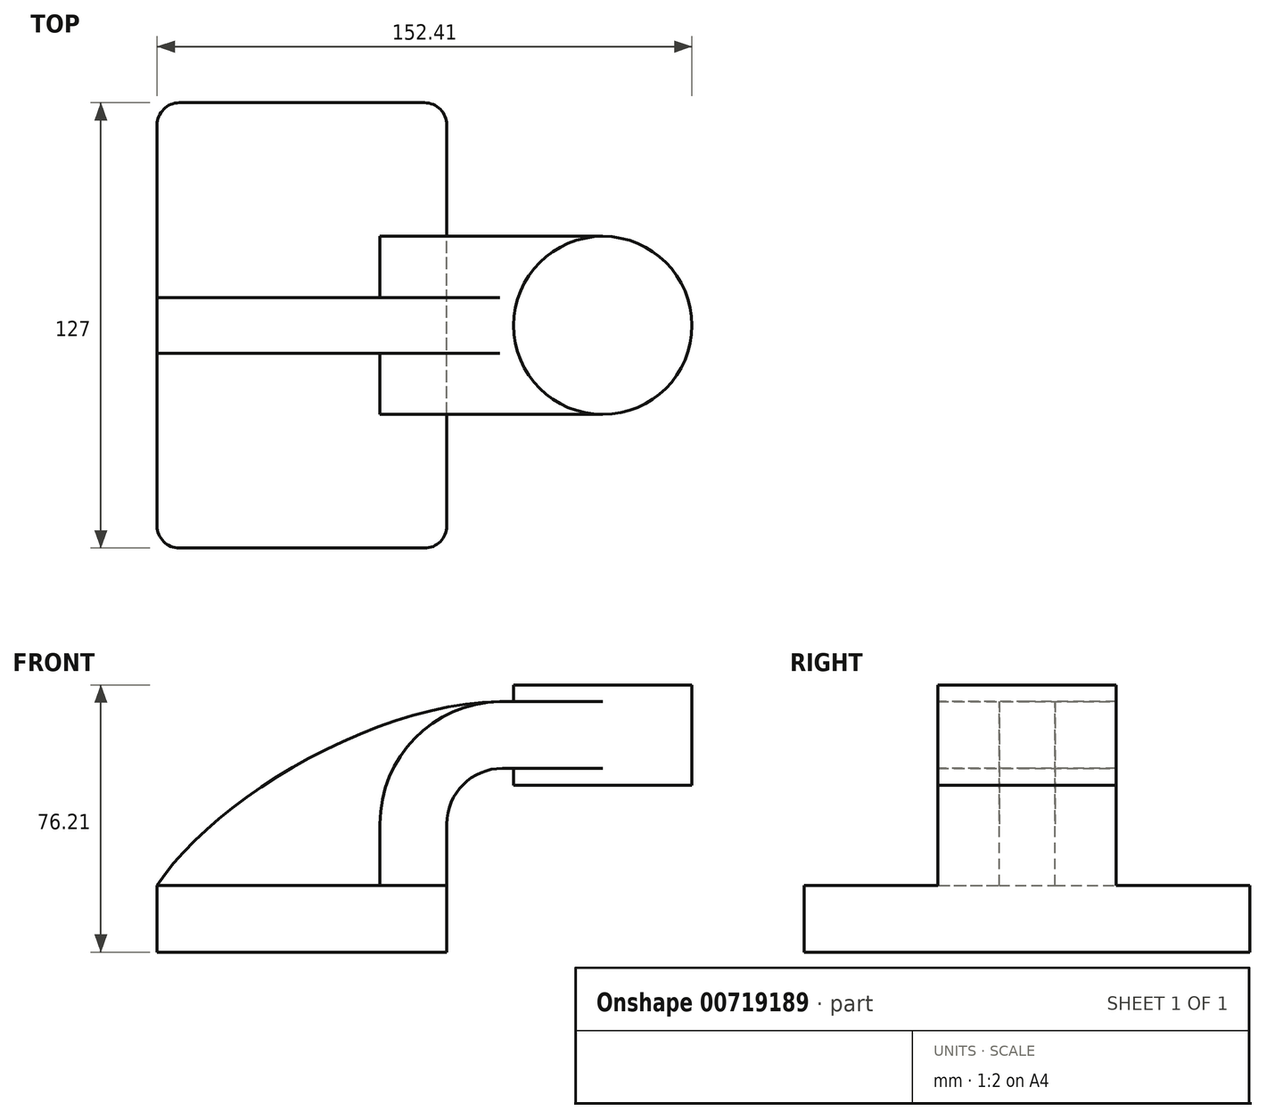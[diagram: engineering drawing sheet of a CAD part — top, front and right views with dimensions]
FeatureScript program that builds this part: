
annotation { "Feature Type Name" : "Feature", "Feature Type Description" : "" }
export const myFeature = defineFeature(function(context is Context, id is Id, definition is map)
    precondition{}
    {
        {
            var Q0;
            Q0=qCreatedBy(makeId("Front.planeOp"),FACE);
            var sketch = newSketch(context, id + "F0", { "sketchPlane" : qUnion([Q0])});
            skLineSegment(sketch, "E0.bottom", {"start": v(-41.28, 9.52) * mm, "end": v(41.27, 9.53) * mm});
            skLineSegment(sketch, "E0.top", {"start": v(-41.28, -9.53) * mm, "end": v(41.28, -9.53) * mm});
            skLineSegment(sketch, "E0.left", {"start": v(-41.28, 9.52) * mm, "end": v(-41.27, -9.53) * mm});
            skLineSegment(sketch, "E0.right", {"start": v(41.28, 9.53) * mm, "end": v(41.28, -9.52) * mm});
            skPoint(sketch, "E0.middle", {"position": v(0, 0) * mm});
            skLineSegment(sketch, "E1.bottom", {"start": v(111.12, 38.1) * mm, "end": v(60.32, 38.1) * mm});
            skLineSegment(sketch, "E1.top", {"start": v(111.12, 66.68) * mm, "end": v(60.32, 66.67) * mm});
            skLineSegment(sketch, "E1.left", {"start": v(111.12, 38.1) * mm, "end": v(111.12, 66.68) * mm});
            skLineSegment(sketch, "E1.right", {"start": v(60.32, 38.1) * mm, "end": v(60.32, 66.67) * mm});
            skPoint(sketch, "E1.middle", {"position": v(85.72, 52.39) * mm});
            skLineSegment(sketch, "E2", {"start": v(41.27, 9.53) * mm, "end": v(41.27, 27) * mm});
            skArc(sketch, "E3", {"start": v(41.27, 27) * mm, "mid": v(45.92, 38.23) * mm, "end": v(57.15, 42.88) * mm});
            skLineSegment(sketch, "E4", {"start": v(57.15, 42.88) * mm, "end": v(85.72, 42.88) * mm});
            skArc(sketch, "E5.0", {"start": v(22.22, 27) * mm, "mid": v(32.45, 51.7) * mm, "end": v(57.15, 61.93) * mm});
            skLineSegment(sketch, "E5.1", {"start": v(22.22, 9.53) * mm, "end": v(22.22, 27) * mm});
            skLineSegment(sketch, "E6.0", {"start": v(57.15, 61.93) * mm, "end": v(85.73, 61.93) * mm});
            skLineSegment(sketch, "E7", {"start": v(85.72, 38.1) * mm, "end": v(85.72, 66.68) * mm});
            skFitSpline(sketch, "E8", {"points": [v(-41.28, 9.52) * mm, v(57.15, 61.93) * mm], "startDerivative": vector(47.24, 72.44) * mm, "endDerivative": vector(110, 0.7) * mm});
            skSolve(sketch);
        }
        {
            var Q0;
            Q0=makeQuery(id+"F0.imprint","IMPRINT",FACE,{"disambiguationData":[TD([[makeQuery(id+"F0.imprint","IMPRINT",EDGE,{"derivedFrom":sQuery(id+"F0.wireOp",EDGE,"E0.top")}),1.0]])]});
            extrude(context, id + "F1", {"entities" : qUnion([Q0]), "endBound" : BoundingType.SYMMETRIC, "depth" : 127 * mm, "offsetDistance" : 25.4 * mm});
        }
        {
            var Q0;
            {var subQ1=sQuery(id+"F0.wireOp",EDGE,"E2");Q0=makeQuery(id+"F0.imprint","IMPRINT",FACE,{"disambiguationData":[TD([[makeQuery(id+"F0.imprint","IMPRINT",EDGE,{"derivedFrom":subQ1}),1.0]])]});}
            var Q1;
            {var subQ0=sQuery(id+"F0.wireOp",EDGE,"E4");var subQ1=sQuery(id+"F0.wireOp",EDGE,"E1.right");var subQ2=makeQuery(id+"F0.imprint","INTERSECT",VERTEX,{"derivedFrom":[subQ1,subQ0]});Q1=makeQuery(id+"F0.imprint","IMPRINT",FACE,{"disambiguationData":[TD([[makeQuery(id+"F0.imprint","IMPRINT",EDGE,{"disambiguationData":[TD([[subQ2,-1.0]])],"derivedFrom":subQ1}),-1.0]])]});}
            extrude(context, id + "F2", {"entities" : qUnion([Q0, Q1]), "operationType" : NewBodyOperationType.ADD, "endBound" : BoundingType.SYMMETRIC, "depth" : 50.8 * mm, "offsetDistance" : 25.4 * mm});
        }
        {
            var Q0;
            {var subQ3=sQuery(id+"F0.wireOp",EDGE,"E5.1");Q0=makeQuery(id+"F0.imprint","IMPRINT",FACE,{"disambiguationData":[TD([[makeQuery(id+"F0.imprint","IMPRINT",EDGE,{"derivedFrom":subQ3}),1.0]])]});}
            extrude(context, id + "F3", {"entities" : qUnion([Q0]), "operationType" : NewBodyOperationType.ADD, "endBound" : BoundingType.SYMMETRIC, "depth" : 15.88 * mm, "offsetDistance" : 25.4 * mm});
        }
        {
            var Q0;
            {var subQ0=sQuery(id+"F0.wireOp",EDGE,"E1.left");Q0=makeQuery(id+"F0.imprint","IMPRINT",FACE,{"disambiguationData":[TD([[makeQuery(id+"F0.imprint","IMPRINT",EDGE,{"derivedFrom":subQ0}),1.0]])]});}
            var Q1;
            Q1=sQuery(id+"F0.wireOp",EDGE,"E7");
            revolve(context, id + "F4", {"operationType" : NewBodyOperationType.ADD, "surfaceOperationType" : NewSurfaceOperationType.NEW, "entities" : qUnion([Q0]), "axis" : qUnion([Q1]), "revolveType" : RevolveType.FULL});
        }
        {
            var Q0;
            Q0=makeQuery(id+"F1.opExtrude","CAP_EDGE",EDGE,{"disambiguationData":[OSD([sQuery(id+"F0.wireOp",EDGE,"E0.left")])],"isStart":false});
            var Q1;
            Q1=makeQuery(id+"F1.opExtrude","CAP_EDGE",EDGE,{"disambiguationData":[OSD([sQuery(id+"F0.wireOp",EDGE,"E0.right")])],"isStart":false});
            var Q2;
            Q2=makeQuery(id+"F1.opExtrude","CAP_EDGE",EDGE,{"disambiguationData":[OSD([sQuery(id+"F0.wireOp",EDGE,"E0.right")])],"isStart":true});
            var Q3;
            Q3=makeQuery(id+"F1.opExtrude","CAP_EDGE",EDGE,{"disambiguationData":[OSD([sQuery(id+"F0.wireOp",EDGE,"E0.left")])],"isStart":true});
            fillet(context, id + "F5", {"entities" : qUnion([Q0, Q1, Q2, Q3]), "radius" : 6.35 * mm, "tangentPropagation" : true, "allowEdgeOverflow" : false});
        }
    });
